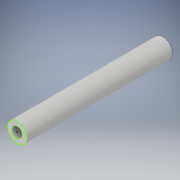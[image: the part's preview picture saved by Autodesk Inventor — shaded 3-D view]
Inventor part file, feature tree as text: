
AUTODESK INVENTOR PART (.ipt)
format: ipt  version: 2017 (Build 210142000, 142)  size: 94,720 bytes
history: native  units: in
note: dims shown in document units (in); Inventor stores cm internally (conversion verified against a paired STEP export)
features: sketch x2, extrude x1
ambient origin geometry x8: Origin, YZ Plane, XZ Plane, XY Plane, X Axis, Y Axis, Z Axis, Center Point
bodies: Solid1 (feature_tree)
feature tree (3):
  extrude  "Extrusion1"  [1 undecoded]
  sketch  "Sketch3"
  sketch  "Sketch1"  dims[d0=3.75in d1=0.0in]
note: 1 required parameter value undecoded (feature->parameter linkage not recoverable at this tier; creation-order binding heuristic only, values carry confidence <= 0.55)
